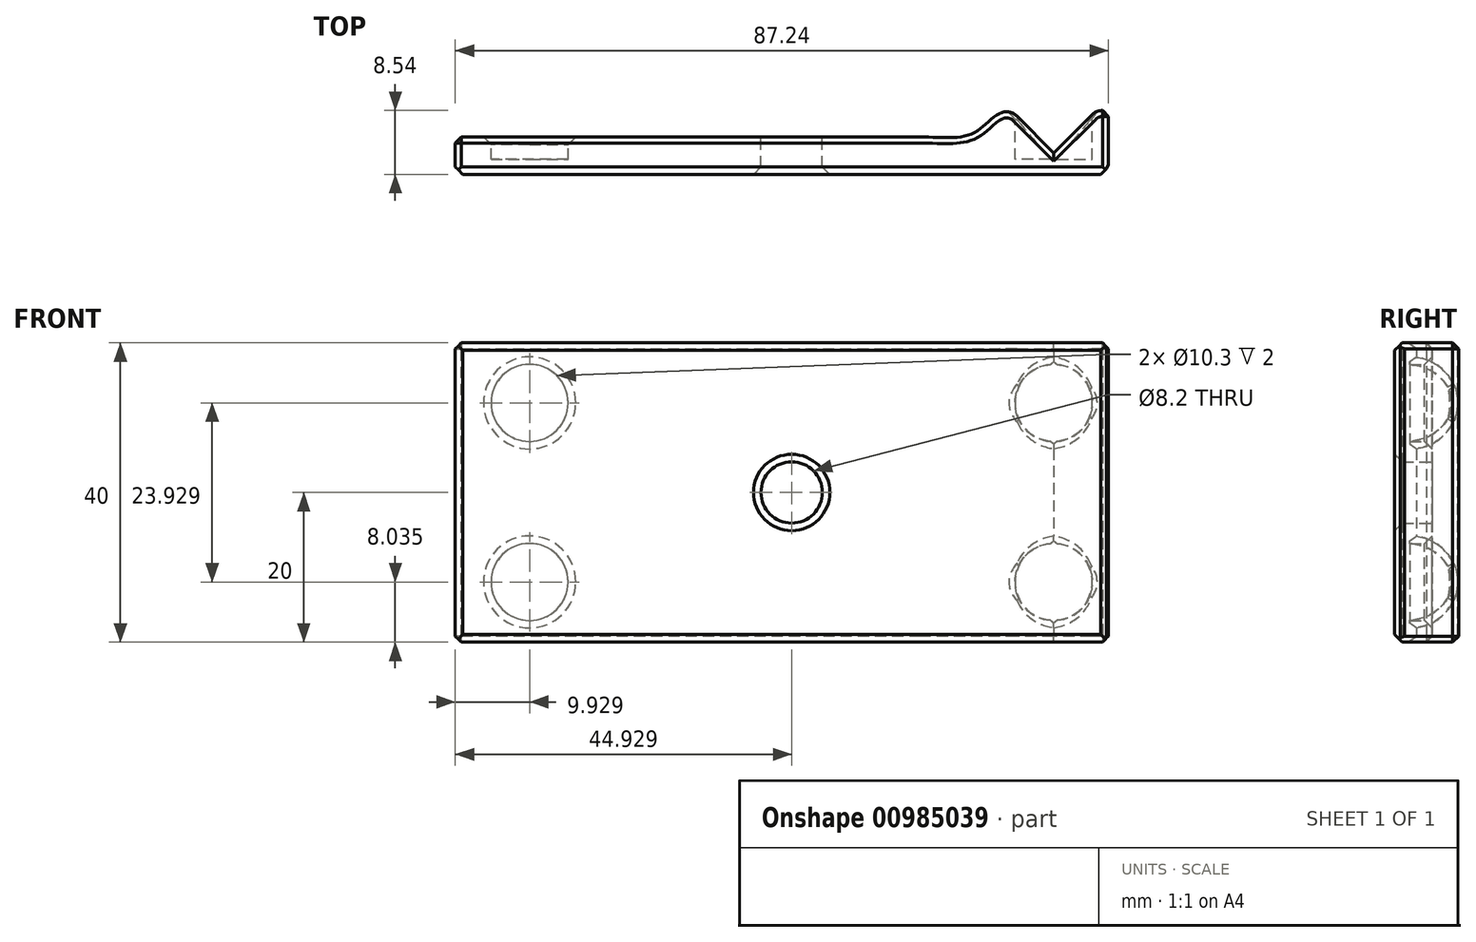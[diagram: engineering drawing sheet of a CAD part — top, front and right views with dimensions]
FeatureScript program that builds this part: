
annotation { "Feature Type Name" : "Feature", "Feature Type Description" : "" }
export const myFeature = defineFeature(function(context is Context, id is Id, definition is map)
    precondition{}
    {
        {
            var Q0;
            Q0=qCreatedBy(makeId("Top.planeOp"),FACE);
            var sketch = newSketch(context, id + "F0", { "sketchPlane" : qUnion([Q0])});
            skLineSegment(sketch, "E0", {"start": v(25.08, 0) * mm, "end": v(25.08, 8.54) * mm});
            skLineSegment(sketch, "E1", {"start": v(25.08, 8.54) * mm, "end": v(24.25, 8.54) * mm});
            skLineSegment(sketch, "E2", {"start": v(22.84, 7.95) * mm, "end": v(17.77, 2.88) * mm});
            skLineSegment(sketch, "E3", {"start": v(17.77, 2.88) * mm, "end": v(12.86, 7.79) * mm});
            skLineSegment(sketch, "E4", {"start": v(0, 0) * mm, "end": v(25.08, 0) * mm});
            skCircle(sketch, "E5", {"center": v(17.77, 8.54) * mm, "radius": 4 * mm, "construction": true});
            skFitSpline(sketch, "E6", {"points": [v(12.11, 8.54) * mm, v(7.15, 5.6) * mm, v(0, 5) * mm], "startDerivative": vector(-14, 0) * mm, "endDerivative": vector(-14.16, 0) * mm});
            skLineSegment(sketch, "E7", {"start": v(0, 5) * mm, "end": v(2.49, 5) * mm, "construction": true});
            skLineSegment(sketch, "E8", {"start": v(12.11, 8.54) * mm, "end": v(9.9, 8.54) * mm, "construction": true});
            skArc(sketch, "E9.filletArc", {"start": v(12.86, 7.79) * mm, "mid": v(11.76, 8.35) * mm, "end": v(10.54, 8.15) * mm});
            skPoint(sketch, "E10.visualSharp", {"position": v(23.43, 8.54) * mm});
            skArc(sketch, "E10.filletArc", {"start": v(24.25, 8.54) * mm, "mid": v(23.49, 8.39) * mm, "end": v(22.84, 7.95) * mm});
            skLineSegment(sketch, "E11", {"start": v(0, -4.1) * mm, "end": v(0, 11.2) * mm, "construction": true});
            skLineSegment(sketch, "E12", {"start": v(0, 5) * mm, "end": v(-62.16, 5) * mm});
            skLineSegment(sketch, "E13", {"start": v(-62.16, 5) * mm, "end": v(-62.16, 0) * mm});
            skLineSegment(sketch, "E14", {"start": v(-62.16, 0) * mm, "end": v(0, 0) * mm});
            skLineSegment(sketch, "E15", {"start": v(-57.23, 5) * mm, "end": v(-47.23, 5) * mm, "construction": true});
            skPoint(sketch, "E16", {"position": v(-52.23, 5) * mm});
            skSolve(sketch);
        }
        {
            var Q0;
            Q0 = qSketchRegion(id + "F0", true);
            extrude(context, id + "F1", {"entities" : qUnion([Q0]), "endBound" : BoundingType.SYMMETRIC, "depth" : 40 * mm, "offsetDistance" : 25 * mm});
        }
        {
            var Q0;
            Q0=makeQuery(id+"F1.opExtrude","SWEPT_FACE",FACE,{"disambiguationData":[OSD([sQuery(id+"F0.wireOp",EDGE,"E12")])]});
            var sketch = newSketch(context, id + "F2", { "sketchPlane" : qUnion([Q0])});
            skPoint(sketch, "E17.0", {"position": v(52.23, 0) * mm});
            skPoint(sketch, "E18.0", {"position": v(47.23, 0) * mm});
            skPoint(sketch, "E19.0", {"position": v(57.23, 0) * mm});
            skLineSegment(sketch, "E20.0", {"start": v(-17.77, 20) * mm, "end": v(-17.77, -20) * mm, "construction": true});
            skCircle(sketch, "E21", {"center": v(-17.77, 11.96) * mm, "radius": 5.15 * mm});
            skCircle(sketch, "E22", {"center": v(-17.77, -11.96) * mm, "radius": 5.15 * mm});
            skCircle(sketch, "E23", {"center": v(52.23, -11.96) * mm, "radius": 5.15 * mm});
            skCircle(sketch, "E24", {"center": v(52.23, 11.96) * mm, "radius": 5.15 * mm});
            skLineSegment(sketch, "E25", {"start": v(-17.77, -11.96) * mm, "end": v(52.23, -11.96) * mm, "construction": true});
            skLineSegment(sketch, "E26", {"start": v(52.23, 11.96) * mm, "end": v(-17.77, 11.96) * mm, "construction": true});
            skLineSegment(sketch, "E27", {"start": v(-17.77, 0) * mm, "end": v(-17.77, 11.96) * mm, "construction": true});
            skLineSegment(sketch, "E28", {"start": v(-17.77, 0) * mm, "end": v(-17.77, -11.96) * mm, "construction": true});
            skLineSegment(sketch, "E29", {"start": v(52.23, 0) * mm, "end": v(52.23, -11.96) * mm, "construction": true});
            skLineSegment(sketch, "E30", {"start": v(52.23, 0) * mm, "end": v(52.23, 11.96) * mm, "construction": true});
            skSolve(sketch);
        }
        {
            var Q0;
            Q0 = qSketchRegion(id + "F2", true);
            extrude(context, id + "F3", {"entities" : qUnion([Q0]), "operationType" : NewBodyOperationType.REMOVE, "oppositeDirection" : true, "depth" : 3 * mm, "offsetDistance" : 25 * mm, "hasSecondDirection" : true, "secondDirectionOppositeDirection" : false, "secondDirectionDepth" : 25 * mm});
        }
        {
            var Q0;
            Q0=makeQuery(id+"F1.opExtrude","SWEPT_FACE",FACE,{"disambiguationData":[OSD([sQuery(id+"F0.wireOp",EDGE,"E12")])]});
            var sketch = newSketch(context, id + "F4", { "sketchPlane" : qUnion([Q0])});
            skCircle(sketch, "E31", {"center": v(17.23, 0) * mm, "radius": 4.1 * mm});
            skPoint(sketch, "E32.0", {"position": v(-17.77, 0) * mm});
            skPoint(sketch, "E33.0", {"position": v(52.23, 0) * mm});
            skLineSegment(sketch, "E34", {"start": v(-17.77, 0) * mm, "end": v(52.23, 0) * mm, "construction": true});
            skSolve(sketch);
        }
        {
            var Q0;
            Q0 = qSketchRegion(id + "F4", true);
            extrude(context, id + "F5", {"entities" : qUnion([Q0]), "operationType" : NewBodyOperationType.REMOVE, "endBound" : BoundingType.THROUGH_ALL, "oppositeDirection" : true, "depth" : 25 * mm, "offsetDistance" : 25 * mm});
        }
        {
            var Q0;
            Q0=makeQuery(id+"F5.boolean.opBoolean","COPY",EDGE,{"derivedFrom":makeQuery(id+"F5.opExtrude","CAP_EDGE",EDGE,{"disambiguationData":[OSD([sQuery(id+"F4.wireOp",EDGE,"E31")])],"isStart":true})});
            var Q1;
            Q1=makeQuery(id+"F3.boolean.opBoolean","INTERSECT",EDGE,{"disambiguationData":[OD(1.0)],"derivedFrom":[makeQuery(id+"F1.opExtrude","SWEPT_FACE",FACE,{"disambiguationData":[OSD([sQuery(id+"F0.wireOp",EDGE,"E3")])]}),makeQuery(id+"F3.opExtrude","SWEPT_FACE",FACE,{"disambiguationData":[OSD([sQuery(id+"F2.wireOp",EDGE,"E21")])]})]});
            var Q2;
            Q2=makeQuery(id+"F3.boolean.opBoolean","INTERSECT",EDGE,{"disambiguationData":[OD(0.0)],"derivedFrom":[makeQuery(id+"F1.opExtrude","SWEPT_FACE",FACE,{"disambiguationData":[OSD([sQuery(id+"F0.wireOp",EDGE,"E3")])]}),makeQuery(id+"F3.opExtrude","SWEPT_FACE",FACE,{"disambiguationData":[OSD([sQuery(id+"F2.wireOp",EDGE,"E21")])]})]});
            var Q3;
            Q3=makeQuery(id+"F3.boolean.opBoolean","INTERSECT",EDGE,{"disambiguationData":[OD(0.0)],"derivedFrom":[makeQuery(id+"F1.opExtrude","SWEPT_FACE",FACE,{"disambiguationData":[OSD([sQuery(id+"F0.wireOp",EDGE,"E2")])]}),makeQuery(id+"F3.opExtrude","SWEPT_FACE",FACE,{"disambiguationData":[OSD([sQuery(id+"F2.wireOp",EDGE,"E21")])]})]});
            var Q4;
            Q4=makeQuery(id+"F3.boolean.opBoolean","INTERSECT",EDGE,{"disambiguationData":[OD(1.0)],"derivedFrom":[makeQuery(id+"F1.opExtrude","SWEPT_FACE",FACE,{"disambiguationData":[OSD([sQuery(id+"F0.wireOp",EDGE,"E2")])]}),makeQuery(id+"F3.opExtrude","SWEPT_FACE",FACE,{"disambiguationData":[OSD([sQuery(id+"F2.wireOp",EDGE,"E21")])]})]});
            var Q5;
            Q5=makeQuery(id+"F3.boolean.opBoolean","INTERSECT",EDGE,{"disambiguationData":[OD(1.0)],"derivedFrom":[makeQuery(id+"F1.opExtrude","SWEPT_FACE",FACE,{"disambiguationData":[OSD([sQuery(id+"F0.wireOp",EDGE,"E3")])]}),makeQuery(id+"F3.opExtrude","SWEPT_FACE",FACE,{"disambiguationData":[OSD([sQuery(id+"F2.wireOp",EDGE,"E22")])]})]});
            var Q6;
            Q6=makeQuery(id+"F3.boolean.opBoolean","INTERSECT",EDGE,{"disambiguationData":[OD(1.0)],"derivedFrom":[makeQuery(id+"F1.opExtrude","SWEPT_FACE",FACE,{"disambiguationData":[OSD([sQuery(id+"F0.wireOp",EDGE,"E2")])]}),makeQuery(id+"F3.opExtrude","SWEPT_FACE",FACE,{"disambiguationData":[OSD([sQuery(id+"F2.wireOp",EDGE,"E22")])]})]});
            var Q7;
            Q7=makeQuery(id+"F3.boolean.opBoolean","INTERSECT",EDGE,{"disambiguationData":[OD(0.0)],"derivedFrom":[makeQuery(id+"F1.opExtrude","SWEPT_FACE",FACE,{"disambiguationData":[OSD([sQuery(id+"F0.wireOp",EDGE,"E2")])]}),makeQuery(id+"F3.opExtrude","SWEPT_FACE",FACE,{"disambiguationData":[OSD([sQuery(id+"F2.wireOp",EDGE,"E22")])]})]});
            var Q8;
            Q8=makeQuery(id+"F3.boolean.opBoolean","INTERSECT",EDGE,{"derivedFrom":[makeQuery(id+"F1.opExtrude","SWEPT_FACE",FACE,{"disambiguationData":[OSD([sQuery(id+"F0.wireOp",EDGE,"E12")])]}),makeQuery(id+"F3.opExtrude","SWEPT_FACE",FACE,{"disambiguationData":[OSD([sQuery(id+"F2.wireOp",EDGE,"E23")])]})]});
            var Q9;
            Q9=makeQuery(id+"F3.boolean.opBoolean","INTERSECT",EDGE,{"derivedFrom":[makeQuery(id+"F1.opExtrude","SWEPT_FACE",FACE,{"disambiguationData":[OSD([sQuery(id+"F0.wireOp",EDGE,"E12")])]}),makeQuery(id+"F3.opExtrude","SWEPT_FACE",FACE,{"disambiguationData":[OSD([sQuery(id+"F2.wireOp",EDGE,"E24")])]})]});
            var Q10;
            Q10=makeQuery(id+"F5.boolean.opBoolean","INTERSECT",EDGE,{"derivedFrom":[makeQuery(id+"F1.opExtrude","SWEPT_FACE",FACE,{"disambiguationData":[OSD([sQuery(id+"F0.wireOp",EDGE,"E4"),sQuery(id+"F0.wireOp",EDGE,"E14")])]}),makeQuery(id+"F5.opExtrude","SWEPT_FACE",FACE,{"disambiguationData":[OSD([sQuery(id+"F4.wireOp",EDGE,"E31")])]})]});
            var Q11;
            Q11=makeQuery(id+"F1.opExtrude","SWEPT_FACE",FACE,{"disambiguationData":[OSD([sQuery(id+"F0.wireOp",EDGE,"E4"),sQuery(id+"F0.wireOp",EDGE,"E14")])]});
            chamfer(context, id + "F6", {"entities" : qUnion([Q0, Q1, Q2, Q3, Q4, Q5, Q6, Q7, Q8, Q9, Q10, Q11]), "width" : 1 * mm, "tangentPropagation" : true});
        }
        {
            var Q0;
            Q0=makeQuery(id+"F1.opExtrude","CAP_EDGE",EDGE,{"disambiguationData":[OSD([sQuery(id+"F0.wireOp",EDGE,"E2")])],"isStart":true});
            var Q1;
            Q1=makeQuery(id+"F1.opExtrude","CAP_EDGE",EDGE,{"disambiguationData":[OSD([sQuery(id+"F0.wireOp",EDGE,"E3")])],"isStart":true});
            var Q2;
            Q2=makeQuery(id+"F1.opExtrude","CAP_EDGE",EDGE,{"disambiguationData":[OSD([sQuery(id+"F0.wireOp",EDGE,"E2")])],"isStart":false});
            var Q3;
            Q3=makeQuery(id+"F1.opExtrude","CAP_EDGE",EDGE,{"disambiguationData":[OSD([sQuery(id+"F0.wireOp",EDGE,"E3")])],"isStart":false});
            var Q4;
            Q4=makeQuery(id+"F1.opExtrude","CAP_EDGE",EDGE,{"disambiguationData":[OSD([sQuery(id+"F0.wireOp",EDGE,"E13")])],"isStart":false});
            var Q5;
            Q5=makeQuery(id+"F1.opExtrude","CAP_EDGE",EDGE,{"disambiguationData":[OSD([sQuery(id+"F0.wireOp",EDGE,"E13")])],"isStart":true});
            var Q6;
            Q6=makeQuery(id+"F1.opExtrude","SWEPT_EDGE",EDGE,{"disambiguationData":[OSD([sQuery(id+"F0.wireOp",EDGE,"E12"),sQuery(id+"F0.wireOp",EDGE,"E13")])]});
            var Q7;
            Q7=makeQuery(id+"F1.opExtrude","SWEPT_FACE",FACE,{"disambiguationData":[OSD([sQuery(id+"F0.wireOp",EDGE,"E0")])]});
            chamfer(context, id + "F7", {"entities" : qUnion([Q0, Q1, Q2, Q3, Q4, Q5, Q6, Q7]), "width" : .8 * mm, "tangentPropagation" : true});
        }
    });
